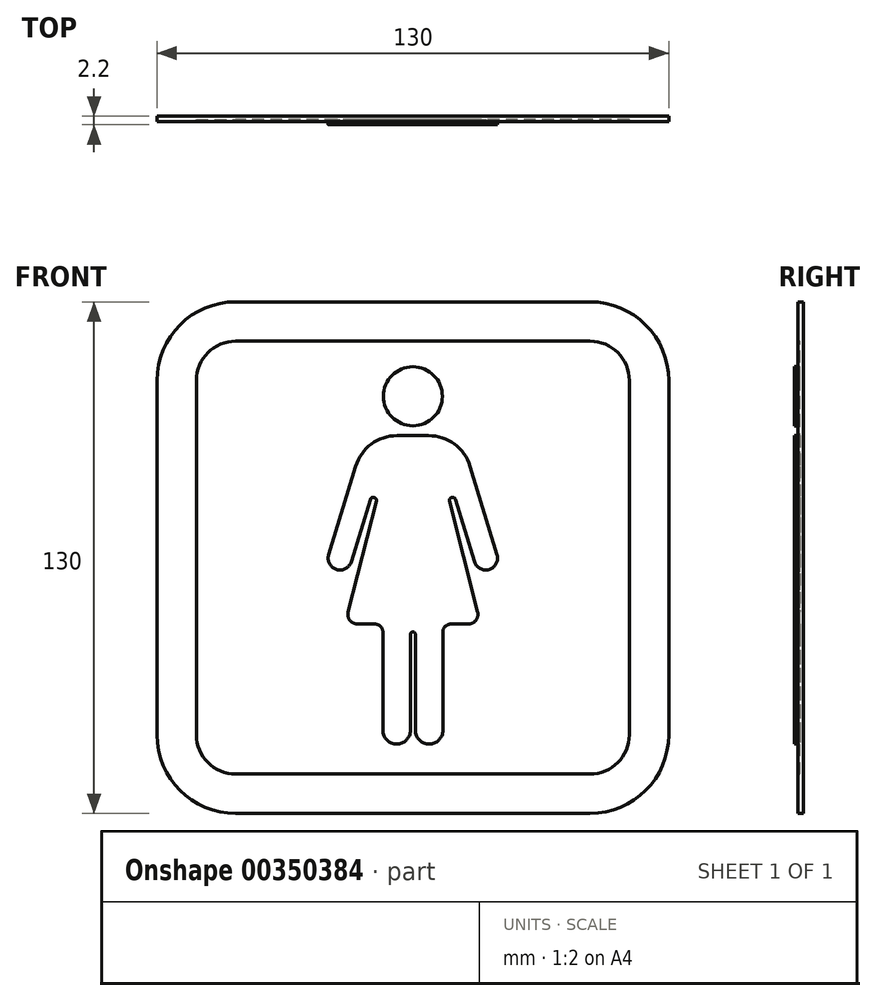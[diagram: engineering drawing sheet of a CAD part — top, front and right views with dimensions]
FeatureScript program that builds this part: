
annotation { "Feature Type Name" : "Feature", "Feature Type Description" : "" }
export const myFeature = defineFeature(function(context is Context, id is Id, definition is map)
    precondition{}
    {
        {
            var Q0;
            Q0=qCreatedBy(makeId("Front.planeOp"),FACE);
            var sketch = newSketch(context, id + "F0", { "sketchPlane" : qUnion([Q0])});
            skLineSegment(sketch, "E0.bottom", {"start": v(20, 0) * mm, "end": v(65, 0) * mm});
            skLineSegment(sketch, "E0.top", {"start": v(20, 130) * mm, "end": v(65, 130) * mm});
            skLineSegment(sketch, "E0.left", {"start": v(0, 20) * mm, "end": v(0, 110) * mm});
            skArc(sketch, "E1", {"start": v(65, 113.5) * mm, "mid": v(57.5, 106) * mm, "end": v(65, 98.5) * mm});
            skArc(sketch, "E2", {"start": v(61, 96) * mm, "mid": v(54.46, 93.84) * mm, "end": v(50.48, 88.22) * mm});
            skArc(sketch, "E3", {"start": v(43.6, 65.74) * mm, "mid": v(45.6, 62) * mm, "end": v(49.35, 63.99) * mm});
            skArc(sketch, "E4", {"start": v(55.71, 79.34) * mm, "mid": v(55.15, 80.3) * mm, "end": v(54.17, 79.77) * mm});
            skArc(sketch, "E5", {"start": v(57.37, 46.12) * mm, "mid": v(56.79, 47.53) * mm, "end": v(55.37, 48.12) * mm});
            skArc(sketch, "E6", {"start": v(48.55, 51.23) * mm, "mid": v(49, 49.08) * mm, "end": v(50.97, 48.12) * mm});
            skArc(sketch, "E7", {"start": v(57.37, 21.12) * mm, "mid": v(60.87, 17.62) * mm, "end": v(64.37, 21.12) * mm});
            skLineSegment(sketch, "E8", {"start": v(61, 96) * mm, "end": v(65, 96) * mm});
            skLineSegment(sketch, "E9", {"start": v(50.48, 88.22) * mm, "end": v(43.6, 65.74) * mm});
            skLineSegment(sketch, "E10", {"start": v(54.17, 79.77) * mm, "end": v(49.35, 63.99) * mm});
            skLineSegment(sketch, "E11", {"start": v(55.71, 79.34) * mm, "end": v(48.55, 51.23) * mm});
            skLineSegment(sketch, "E12", {"start": v(50.97, 48.12) * mm, "end": v(55.37, 48.12) * mm});
            skLineSegment(sketch, "E13", {"start": v(57.37, 46.12) * mm, "end": v(57.37, 21.12) * mm});
            skLineSegment(sketch, "E14", {"start": v(64.37, 45.49) * mm, "end": v(64.37, 21.12) * mm});
            skArc(sketch, "E15", {"start": v(65, 46.12) * mm, "mid": v(64.56, 45.93) * mm, "end": v(64.37, 45.49) * mm});
            skArc(sketch, "E16", {"start": v(0, 20) * mm, "mid": v(5.86, 5.86) * mm, "end": v(20, 0) * mm});
            skArc(sketch, "E17", {"start": v(20, 130) * mm, "mid": v(5.86, 124.14) * mm, "end": v(0, 110) * mm});
            skPoint(sketch, "E18.orphan", {"position": v(0, 130) * mm});
            skPoint(sketch, "E19.orphan", {"position": v(0, 0) * mm});
            skArc(sketch, "E20.MirrorCS", {"start": v(65, 113.5) * mm, "mid": v(72.5, 106) * mm, "end": v(65, 98.5) * mm});
            skArc(sketch, "E21.MirrorCS", {"start": v(110, 130) * mm, "mid": v(124.14, 124.14) * mm, "end": v(130, 110) * mm});
            skLineSegment(sketch, "E22.MirrorCS", {"start": v(110, 130) * mm, "end": v(65, 130) * mm});
            skLineSegment(sketch, "E23.MirrorCS", {"start": v(130, 20) * mm, "end": v(130, 110) * mm});
            skArc(sketch, "E24.MirrorCS", {"start": v(130, 20) * mm, "mid": v(124.14, 5.86) * mm, "end": v(110, 0) * mm});
            skLineSegment(sketch, "E25.MirrorCS", {"start": v(110, 0) * mm, "end": v(65, 0) * mm});
            skLineSegment(sketch, "E26.MirrorCS", {"start": v(65.63, 45.49) * mm, "end": v(65.63, 21.12) * mm});
            skArc(sketch, "E27.MirrorCS", {"start": v(65, 46.12) * mm, "mid": v(65.44, 45.93) * mm, "end": v(65.63, 45.49) * mm});
            skArc(sketch, "E28.MirrorCS", {"start": v(72.63, 46.12) * mm, "mid": v(73.21, 47.53) * mm, "end": v(74.63, 48.12) * mm});
            skLineSegment(sketch, "E29.MirrorCS", {"start": v(72.63, 46.12) * mm, "end": v(72.63, 21.12) * mm});
            skArc(sketch, "E30.MirrorCS", {"start": v(72.63, 21.12) * mm, "mid": v(69.13, 17.62) * mm, "end": v(65.63, 21.12) * mm});
            skLineSegment(sketch, "E31.MirrorCS", {"start": v(79.03, 48.12) * mm, "end": v(74.63, 48.12) * mm});
            skArc(sketch, "E32.MirrorCS", {"start": v(81.45, 51.23) * mm, "mid": v(81, 49.08) * mm, "end": v(79.03, 48.12) * mm});
            skLineSegment(sketch, "E33.MirrorCS", {"start": v(74.29, 79.34) * mm, "end": v(81.45, 51.23) * mm});
            skArc(sketch, "E34.MirrorCS", {"start": v(86.4, 65.74) * mm, "mid": v(84.4, 62) * mm, "end": v(80.65, 63.99) * mm});
            skLineSegment(sketch, "E35.MirrorCS", {"start": v(75.83, 79.77) * mm, "end": v(80.65, 63.99) * mm});
            skLineSegment(sketch, "E36.MirrorCS", {"start": v(79.52, 88.22) * mm, "end": v(86.4, 65.74) * mm});
            skArc(sketch, "E37.MirrorCS", {"start": v(69, 96) * mm, "mid": v(75.54, 93.84) * mm, "end": v(79.52, 88.22) * mm});
            skLineSegment(sketch, "E38.MirrorCS", {"start": v(69, 96) * mm, "end": v(65, 96) * mm});
            skLineSegment(sketch, "E39.0", {"start": v(110, 120) * mm, "end": v(65, 120) * mm});
            skLineSegment(sketch, "E39.1", {"start": v(20, 120) * mm, "end": v(65, 120) * mm});
            skArc(sketch, "E39.2", {"start": v(110, 120) * mm, "mid": v(117.07, 117.07) * mm, "end": v(120, 110) * mm});
            skArc(sketch, "E39.3", {"start": v(20, 120) * mm, "mid": v(12.93, 117.07) * mm, "end": v(10, 110) * mm});
            skLineSegment(sketch, "E39.4", {"start": v(10, 20) * mm, "end": v(10, 110) * mm});
            skArc(sketch, "E39.5", {"start": v(10, 20) * mm, "mid": v(12.93, 12.93) * mm, "end": v(20, 10) * mm});
            skLineSegment(sketch, "E39.6", {"start": v(120, 20) * mm, "end": v(120, 110) * mm});
            skArc(sketch, "E39.7", {"start": v(120, 20) * mm, "mid": v(117.07, 12.93) * mm, "end": v(110, 10) * mm});
            skLineSegment(sketch, "E39.8", {"start": v(110, 10) * mm, "end": v(65, 10) * mm});
            skLineSegment(sketch, "E39.9", {"start": v(20, 10) * mm, "end": v(65, 10) * mm});
            skArc(sketch, "E40.MirrorCS", {"start": v(74.29, 79.34) * mm, "mid": v(74.85, 80.3) * mm, "end": v(75.83, 79.77) * mm});
            skSolve(sketch);
        }
        {
            var Q0;
            Q0=makeQuery(id+"F0.imprint","IMPRINT",FACE,{"disambiguationData":[TD([[makeQuery(id+"F0.imprint","IMPRINT",EDGE,{"derivedFrom":sQuery(id+"F0.wireOp",EDGE,"E0.bottom")}),1.0]])]});
            var Q1;
            Q1=makeQuery(id+"F0.imprint","IMPRINT",FACE,{"disambiguationData":[TD([[makeQuery(id+"F0.imprint","IMPRINT",EDGE,{"derivedFrom":sQuery(id+"F0.wireOp",EDGE,"E1")}),-1.0]])]});
            var Q2;
            Q2=makeQuery(id+"F0.imprint","IMPRINT",FACE,{"disambiguationData":[TD([[makeQuery(id+"F0.imprint","IMPRINT",EDGE,{"derivedFrom":sQuery(id+"F0.wireOp",EDGE,"E2")}),1.0]])]});
            var Q3;
            Q3=makeQuery(id+"F0.imprint","IMPRINT",FACE,{"disambiguationData":[TD([[makeQuery(id+"F0.imprint","IMPRINT",EDGE,{"derivedFrom":sQuery(id+"F0.wireOp",EDGE,"E1")}),1.0]])]});
            extrude(context, id + "F1", {"entities" : qUnion([Q0, Q1, Q2, Q3]), "oppositeDirection" : true, "depth" : 0.9 * mm});
        }
        {
            var Q0;
            Q0=makeQuery(id+"F0.imprint","IMPRINT",FACE,{"disambiguationData":[TD([[makeQuery(id+"F0.imprint","IMPRINT",EDGE,{"derivedFrom":sQuery(id+"F0.wireOp",EDGE,"E0.bottom")}),1.0]])]});
            extrude(context, id + "F2", {"entities" : qUnion([Q0]), "operationType" : NewBodyOperationType.ADD, "depth" : 0.5 * mm});
        }
        {
            var Q0;
            Q0=makeQuery(id+"F0.imprint","IMPRINT",FACE,{"disambiguationData":[TD([[makeQuery(id+"F0.imprint","IMPRINT",EDGE,{"derivedFrom":sQuery(id+"F0.wireOp",EDGE,"E1")}),1.0]])]});
            var Q1;
            Q1=makeQuery(id+"F0.imprint","IMPRINT",FACE,{"disambiguationData":[TD([[makeQuery(id+"F0.imprint","IMPRINT",EDGE,{"derivedFrom":sQuery(id+"F0.wireOp",EDGE,"E2")}),1.0]])]});
            extrude(context, id + "F3", {"entities" : qUnion([Q0, Q1]), "operationType" : NewBodyOperationType.ADD, "depth" : 1.3 * mm});
        }
    });
